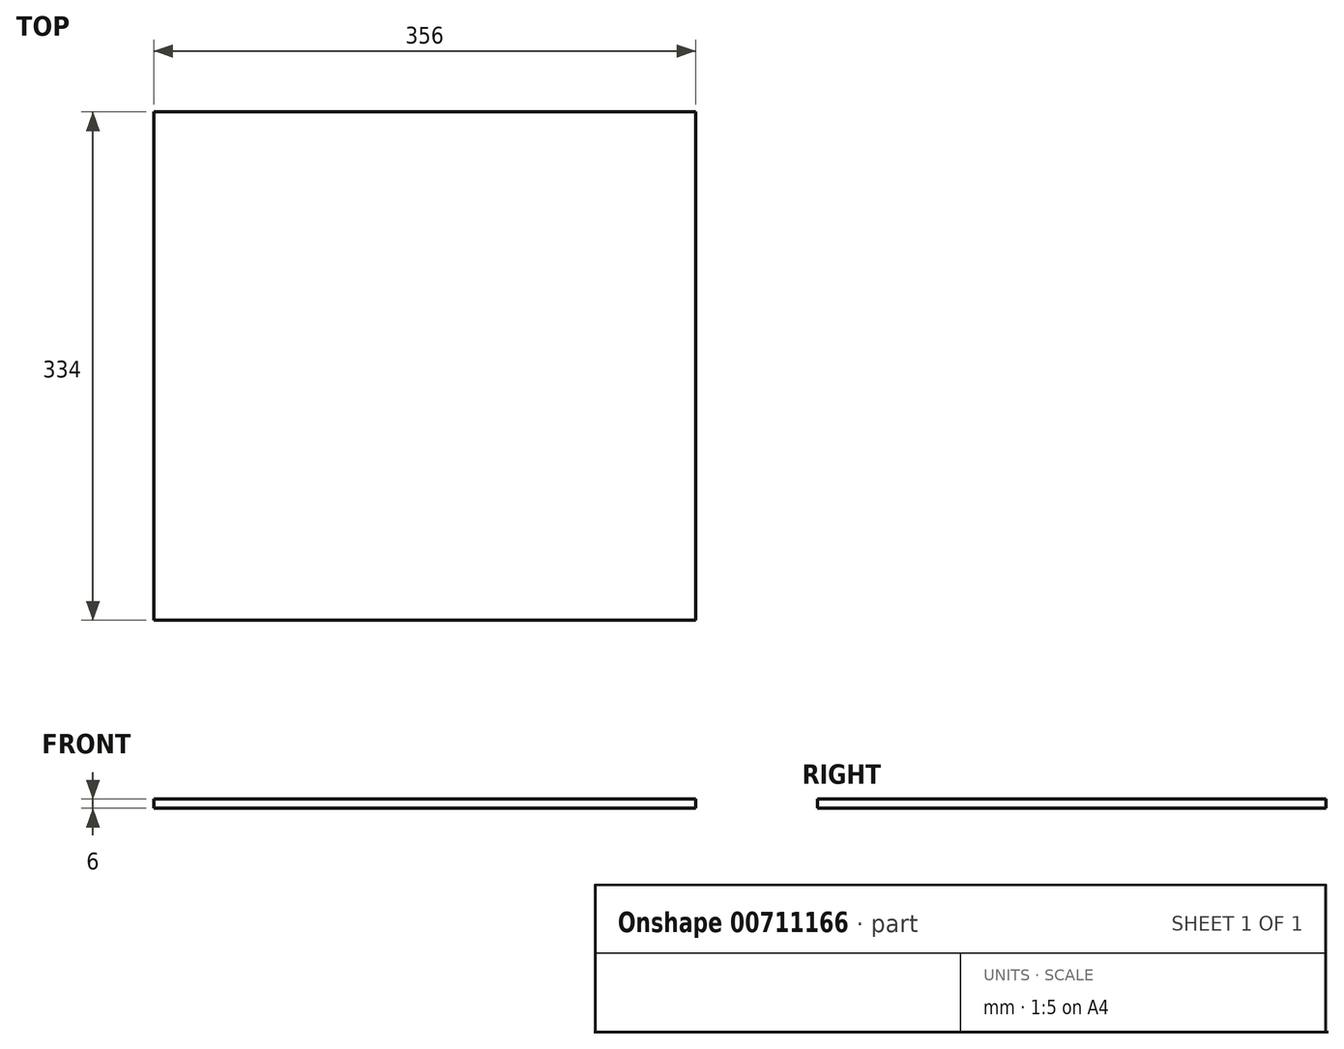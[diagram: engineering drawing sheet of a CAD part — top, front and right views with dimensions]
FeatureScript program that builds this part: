
annotation { "Feature Type Name" : "Feature", "Feature Type Description" : "" }
export const myFeature = defineFeature(function(context is Context, id is Id, definition is map)
    precondition{}
    {
        {
            var Q0;
            Q0=qCreatedBy(makeId("Top.planeOp"),FACE);
            var sketch = newSketch(context, id + "F0", { "sketchPlane" : qUnion([Q0])});
            skLineSegment(sketch, "E0.bottom", {"start": v(-183.85, 114.88) * mm, "end": v(172.15, 114.88) * mm});
            skLineSegment(sketch, "E0.top", {"start": v(-183.85, -219.12) * mm, "end": v(172.15, -219.12) * mm});
            skLineSegment(sketch, "E0.left", {"start": v(-183.85, 114.88) * mm, "end": v(-183.85, -219.12) * mm});
            skLineSegment(sketch, "E0.right", {"start": v(172.15, 114.88) * mm, "end": v(172.15, -219.12) * mm});
            skSolve(sketch);
        }
        {
            var Q0;
            Q0 = qSketchRegion(id + "F0", true);
            extrude(context, id + "F1", {"entities" : qUnion([Q0]), "depth" : 6 * mm, "offsetDistance" : 25 * mm});
        }
    });
